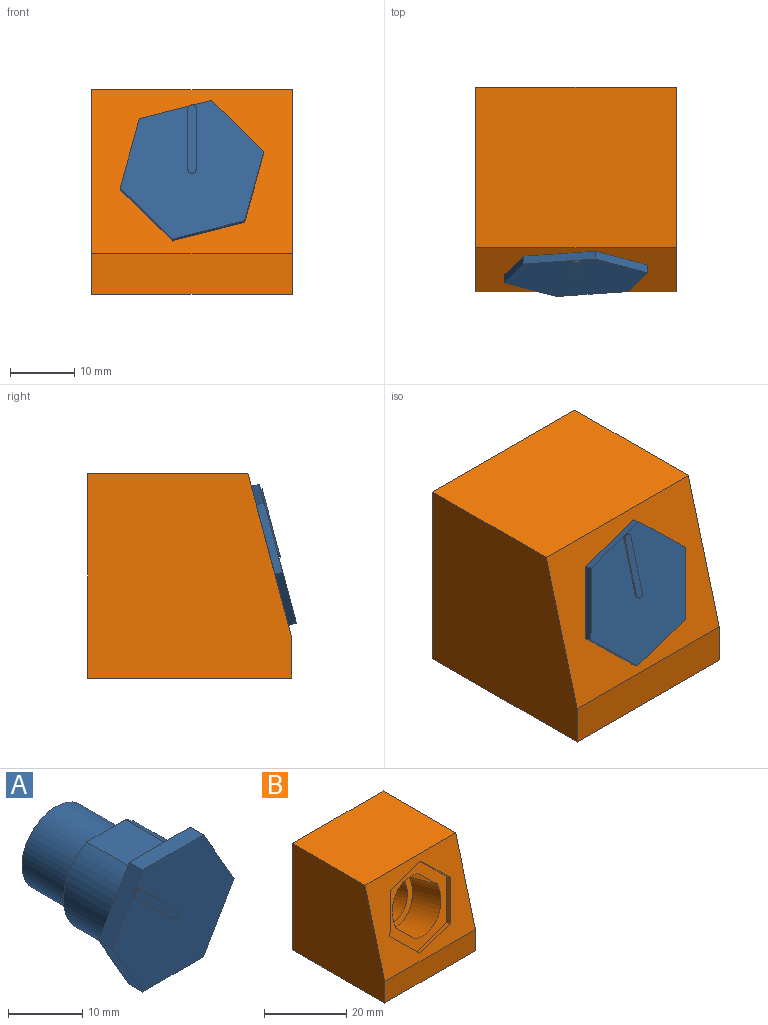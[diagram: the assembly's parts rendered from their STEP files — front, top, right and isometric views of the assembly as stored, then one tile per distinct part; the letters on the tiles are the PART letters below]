
ASSEMBLY  parts=2 mates=1
PART A: 20 faces, bbox 23.2x22.5x20.1 mm
  f0: plane 23.15x20.05mm, normal (0,-1,0), area 334.5mm2, adj f2,f3,f4,f5,f6,f7,f15,f16
  f1: plane 23.15x20.05mm, normal (0,1,0), area 149.6mm2, adj f2,f3,f4,f5,f6,f7,f8,f9
  f2: plane 10.03x5.79mm, normal (-0.87,0,-0.5), area 29.4mm2, adj f0,f1,f3,f7
  f3: plane 11.58x2.54mm, normal (0,0,-1), area 29.4mm2, adj f0,f1,f2,f4
  f4: plane 10.03x5.79mm, normal (0.87,0,-0.5), area 29.4mm2, adj f0,f1,f3,f5
  f5: plane 10.03x5.79mm, normal (0.87,0,0.5), area 29.4mm2, adj f0,f1,f4,f6
  f6: plane 11.58x2.54mm, normal (0,0,1), area 29.4mm2, adj f0,f1,f5,f7
  f7: plane 10.03x5.79mm, normal (-0.87,0,0.5), area 29.4mm2, adj f0,f1,f2,f6
  f8: plane 10.16x7.33mm, normal (0,0,1), area 74.4mm2, adj f1,f9,f11,f12
  f9: cylinder r=8.12mm len=14.49mm, axis (0,-1,0), area 182mm2, adj f1,f8,f10,f12
  f10: plane 10.16x7.33mm, normal (0,0,-1), area 74.4mm2, adj f1,f9,f11,f12
  f11: cylinder r=8.12mm len=14.49mm, axis (0,-1,0), area 182mm2, adj f1,f8,f10,f12
  f12: plane 16.24x14.49mm, normal (0,1,0), area 67.7mm2, adj f8,f9,f10,f11,f13
  f13: cylinder r=6.45mm len=12.91mm, axis (0,-1,0), area 386.2mm2, adj f12,f14
  f14: plane 12.91x12.91mm, normal (0,1,0), area 130.8mm2, adj f13
  f15: cylinder r=0.64mm len=1.08mm, axis (0,1,0), area 0.5mm2, adj f0,f16,f18,f19
  f16: plane 6.87x6.87mm, normal (-0.71,0,-0.71), area 2.5mm2, adj f0,f15,f17,f19
  f17: cylinder r=0.64mm len=1.08mm, axis (0,1,0), area 0.5mm2, adj f0,f16,f18,f19
  f18: plane 6.87x6.87mm, normal (0.71,0,0.71), area 2.5mm2, adj f0,f15,f17,f19
  f19: plane 8.14x8.14mm, normal (0,-1,0), area 13.6mm2, adj f15,f16,f17,f18
PART B: 21 faces, bbox 31.3x31.8x31.8 mm
  f0: plane 31.25x25.4mm, normal (0,-0.97,0.26), area 473.6mm2, adj f1,f2,f4,f5,f8,f9,f10,f11
  f1: plane 31.25x6.35mm, normal (0,-1,0), area 198.4mm2, adj f0,f2,f4,f6
  f2: plane 31.75x31.75mm, normal (1,0,0), area 921.6mm2, adj f0,f1,f3,f5,f6
  f3: plane 31.75x31.25mm, normal (0,1,0), area 992.2mm2, adj f2,f4,f5,f6
  f4: plane 31.75x31.75mm, normal (-1,0,0), area 921.6mm2, adj f0,f1,f3,f5,f6
  f5: plane 31.25x24.94mm, normal (0,0,1), area 779.5mm2, adj f0,f2,f3,f4
  f6: plane 31.75x31.25mm, normal (0,0,-1), area 992.2mm2, adj f1,f2,f3,f4
  f7: plane 22.37x21.59mm, normal (0,-0.97,0.26), area 149.6mm2, adj f8,f9,f10,f11,f12,f13,f14,f15
  f8: plane 11.13x4.12mm, normal (0.97,-0.07,-0.25), area 14.7mm2, adj f0,f7,f9,f13
  f9: plane 8.25x8.18mm, normal (0.71,0.18,0.68), area 14.7mm2, adj f0,f7,f8,f10
  f10: plane 11.19x3.21mm, normal (-0.26,0.25,0.93), area 14.7mm2, adj f0,f7,f9,f11
  f11: plane 11.13x4.12mm, normal (-0.97,0.07,0.25), area 14.7mm2, adj f0,f7,f10,f12
  f12: plane 8.25x8.18mm, normal (-0.71,-0.18,-0.68), area 14.7mm2, adj f0,f7,f11,f13
  f13: plane 11.19x3.21mm, normal (0.26,-0.25,-0.93), area 14.7mm2, adj f0,f7,f8,f12
  f14: plane 11.16x7.64mm, normal (-0.71,-0.18,-0.68), area 74.4mm2, adj f7,f15,f17,f18
  f15: cylinder r=8.12mm len=12.91mm, axis (0,-0.97,0.26), area 182mm2, adj f7,f14,f16,f18
  f16: plane 11.16x7.64mm, normal (0.71,0.18,0.68), area 74.4mm2, adj f7,f15,f17,f18
  f17: cylinder r=8.12mm len=12.91mm, axis (0,-0.97,0.26), area 182mm2, adj f7,f14,f16,f18
  f18: plane 16.24x15.69mm, normal (0,-0.97,0.26), area 67.7mm2, adj f14,f15,f16,f17,f19
  f19: cylinder r=6.45mm len=14.93mm, axis (0,-0.97,0.26), area 386.2mm2, adj f18,f20
  f20: plane 12.91x12.47mm, normal (0,-0.97,0.26), area 130.8mm2, adj f19
PLACE A rot(axis=(-0.3,0.95,-0.12),47.4deg) t=(-0.01,-11.25,18.69)mm
PLACE B at identity fixed
MATE revolute A.f11 <-> B.f7  axis (0,-0.97,0.26) through (-0.01,-11.25,18.69)mm
